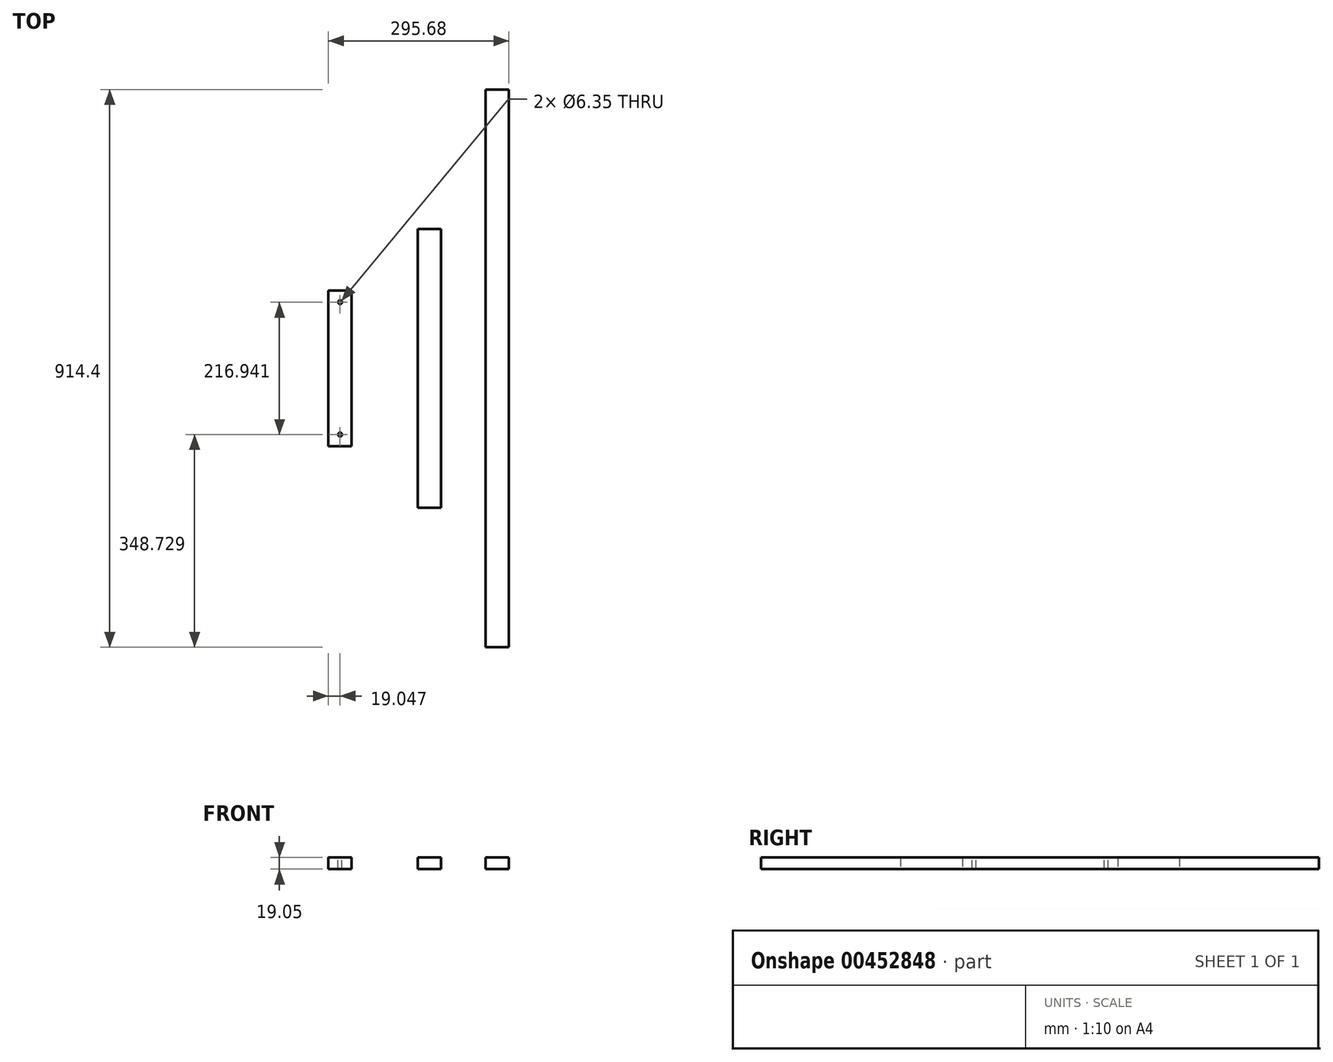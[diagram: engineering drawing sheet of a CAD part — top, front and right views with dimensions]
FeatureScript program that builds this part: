
annotation { "Feature Type Name" : "Feature", "Feature Type Description" : "" }
export const myFeature = defineFeature(function(context is Context, id is Id, definition is map)
    precondition{}
    {
        {
            var Q0;
            Q0=qCreatedBy(makeId("Top.planeOp"),FACE);
            var sketch = newSketch(context, id + "F0", { "sketchPlane" : qUnion([Q0])});
            skLineSegment(sketch, "E0.bottom", {"start": v(19.05, 457.2) * mm, "end": v(-19.05, 457.2) * mm});
            skLineSegment(sketch, "E0.top", {"start": v(19.05, -457.2) * mm, "end": v(-19.05, -457.2) * mm});
            skLineSegment(sketch, "E0.left", {"start": v(19.05, 457.2) * mm, "end": v(19.05, -457.2) * mm});
            skLineSegment(sketch, "E0.right", {"start": v(-19.05, 457.2) * mm, "end": v(-19.05, -457.2) * mm});
            skPoint(sketch, "E0.middle", {"position": v(0, 0) * mm});
            skSolve(sketch);
        }
        {
            var Q0;
            Q0 = qSketchRegion(id + "F0", true);
            extrude(context, id + "F1", {"entities" : qUnion([Q0]), "depth" : 19.05 * mm});
        }
        {
            var Q0;
            Q0=qCreatedBy(makeId("Top.planeOp"),FACE);
            var sketch = newSketch(context, id + "F2", { "sketchPlane" : qUnion([Q0])});
            skLineSegment(sketch, "E1.bottom", {"start": v(-130.43, 228.6) * mm, "end": v(-92.33, 228.6) * mm});
            skLineSegment(sketch, "E1.top", {"start": v(-130.43, -228.6) * mm, "end": v(-92.33, -228.6) * mm});
            skLineSegment(sketch, "E1.left", {"start": v(-130.43, 228.6) * mm, "end": v(-130.43, -228.6) * mm});
            skLineSegment(sketch, "E1.right", {"start": v(-92.33, 228.6) * mm, "end": v(-92.33, -228.6) * mm});
            skPoint(sketch, "E1.middle", {"position": v(-111.38, 0) * mm});
            skSolve(sketch);
        }
        {
            var Q0;
            Q0 = qSketchRegion(id + "F2", true);
            extrude(context, id + "F3", {"entities" : qUnion([Q0]), "depth" : 19.05 * mm});
        }
        {
            var Q0;
            Q0=qCreatedBy(makeId("Top.planeOp"),FACE);
            var sketch = newSketch(context, id + "F5", { "sketchPlane" : qUnion([Q0])});
            skLineSegment(sketch, "E2.bottom", {"start": v(-238.53, 127.52) * mm, "end": v(-276.63, 127.52) * mm});
            skLineSegment(sketch, "E2.top", {"start": v(-238.53, -127.52) * mm, "end": v(-276.63, -127.52) * mm});
            skLineSegment(sketch, "E2.left", {"start": v(-238.53, 127.52) * mm, "end": v(-238.53, -127.52) * mm});
            skLineSegment(sketch, "E2.right", {"start": v(-276.63, 127.52) * mm, "end": v(-276.63, -127.52) * mm});
            skPoint(sketch, "E2.middle", {"position": v(-257.58, 0) * mm});
            skSolve(sketch);
        }
        {
            var Q0;
            Q0 = qSketchRegion(id + "F5", true);
            extrude(context, id + "F6", {"entities" : qUnion([Q0]), "depth" : 19.05 * mm});
        }
        {
            var Q0;
            Q0=makeQuery(id+"F6.opExtrude","CAP_FACE",FACE,{"disambiguationData":[OSD([sQuery(id+"F5.wireOp",EDGE,"E2.bottom"),sQuery(id+"F5.wireOp",EDGE,"E2.top"),sQuery(id+"F5.wireOp",EDGE,"E2.left"),sQuery(id+"F5.wireOp",EDGE,"E2.right")])],"isStart":false});
            var sketch = newSketch(context, id + "F7", { "sketchPlane" : qUnion([Q0])});
            skCircle(sketch, "E3", {"center": v(-257.58, 108.47) * mm, "radius": 3.17 * mm});
            skPoint(sketch, "E3.centerSnap0", {"position": v(-257.58, 127.52) * mm});
            skCircle(sketch, "E4", {"center": v(-257.58, -108.47) * mm, "radius": 3.18 * mm});
            skPoint(sketch, "E4.centerSnap0", {"position": v(-257.58, -127.52) * mm});
            skSolve(sketch);
        }
        {
            var Q0;
            Q0 = qSketchRegion(id + "F7", true);
            extrude(context, id + "F8", {"entities" : qUnion([Q0]), "operationType" : NewBodyOperationType.REMOVE, "endBound" : BoundingType.THROUGH_ALL, "oppositeDirection" : true, "depth" : 25.4 * mm});
        }
    });
